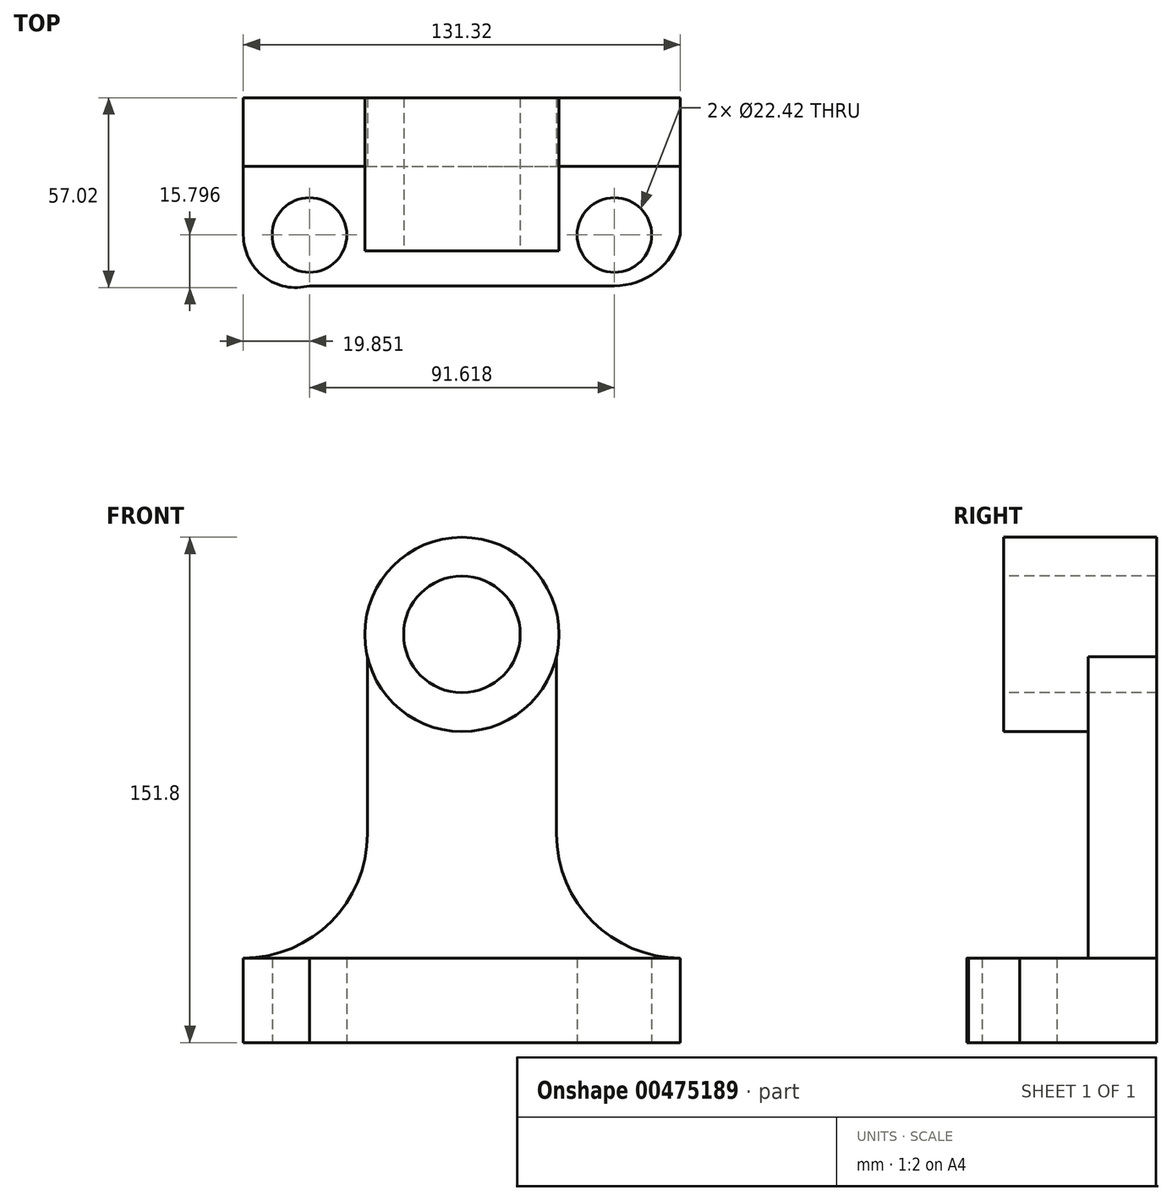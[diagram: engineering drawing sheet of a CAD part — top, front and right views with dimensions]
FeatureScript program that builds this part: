
annotation { "Feature Type Name" : "Feature", "Feature Type Description" : "" }
export const myFeature = defineFeature(function(context is Context, id is Id, definition is map)
    precondition{}
    {
        {
            var Q0;
            Q0=qCreatedBy(makeId("Top.planeOp"),FACE);
            var sketch = newSketch(context, id + "F0", { "sketchPlane" : qUnion([Q0])});
            skLineSegment(sketch, "E0.bottom", {"start": v(65.66, -20.61) * mm, "end": v(-65.66, -20.61) * mm});
            skLineSegment(sketch, "E0.top", {"start": v(65.66, 20.61) * mm, "end": v(-65.66, 20.61) * mm});
            skLineSegment(sketch, "E0.left", {"start": v(65.66, -20.61) * mm, "end": v(65.66, 20.61) * mm});
            skLineSegment(sketch, "E0.right", {"start": v(-65.66, -20.61) * mm, "end": v(-65.66, 20.61) * mm});
            skPoint(sketch, "E0.middle", {"position": v(0, 0) * mm});
            skLineSegment(sketch, "E1.bottom", {"start": v(45.8, -35.88) * mm, "end": v(-45.8, -35.88) * mm});
            skLineSegment(sketch, "E1.left", {"start": v(45.8, -35.88) * mm, "end": v(45.8, -20.61) * mm});
            skLineSegment(sketch, "E1.right", {"start": v(-45.8, -35.88) * mm, "end": v(-45.8, -20.61) * mm});
            skPoint(sketch, "E1.middle", {"position": v(0, -20.61) * mm});
            skPoint(sketch, "E1.top.end.orphan", {"position": v(-45.8, -5.34) * mm});
            skPoint(sketch, "E2.orphan", {"position": v(45.8, -5.34) * mm});
            skArc(sketch, "E3", {"start": v(45.8, -35.88) * mm, "mid": v(58.33, -31.62) * mm, "end": v(65.66, -20.61) * mm});
            skArc(sketch, "E4", {"start": v(-65.66, -20.61) * mm, "mid": v(-59.5, -33.14) * mm, "end": v(-45.8, -35.88) * mm});
            skCircle(sketch, "E5", {"center": v(45.8, -20.61) * mm, "radius": 11.2 * mm});
            skCircle(sketch, "E6", {"center": v(-45.8, -20.61) * mm, "radius": 11.2 * mm});
            skSolve(sketch);
        }
        {
            var Q0;
            {var subQ1=sQuery(id+"F0.wireOp",EDGE,"E1.bottom");Q0=makeQuery(id+"F0.imprint","IMPRINT",FACE,{"disambiguationData":[TD([[makeQuery(id+"F0.imprint","IMPRINT",EDGE,{"derivedFrom":subQ1}),-1.0]])]});}
            var Q1;
            {var subQ0=sQuery(id+"F0.wireOp",EDGE,"E4");Q1=makeQuery(id+"F0.imprint","IMPRINT",FACE,{"disambiguationData":[TD([[makeQuery(id+"F0.imprint","IMPRINT",EDGE,{"derivedFrom":subQ0}),1.0]])]});}
            var Q2;
            {var subQ0=sQuery(id+"F0.wireOp",EDGE,"E3");Q2=makeQuery(id+"F0.imprint","IMPRINT",FACE,{"disambiguationData":[TD([[makeQuery(id+"F0.imprint","IMPRINT",EDGE,{"derivedFrom":subQ0}),1.0]])]});}
            var Q3;
            Q3=makeQuery(id+"F0.imprint","IMPRINT",FACE,{"disambiguationData":[TD([[makeQuery(id+"F0.imprint","IMPRINT",EDGE,{"derivedFrom":sQuery(id+"F0.wireOp",EDGE,"E0.top")}),1.0]])]});
            extrude(context, id + "F1", {"entities" : qUnion([Q0, Q1, Q2, Q3]), "depth" : 25.4 * mm});
        }
        {
            var Q0;
            Q0=qCreatedBy(makeId("Front.planeOp"),FACE);
            var sketch = newSketch(context, id + "F2", { "sketchPlane" : qUnion([Q0])});
            skCircle(sketch, "E7", {"center": v(0, 122.62) * mm, "radius": 17.5 * mm});
            skCircle(sketch, "E8", {"center": v(0, 122.62) * mm, "radius": 29.18 * mm});
            skLineSegment(sketch, "E9.top", {"start": v(-28.4, 25.4) * mm, "end": v(28.4, 25.4) * mm});
            skLineSegment(sketch, "E9.left", {"start": v(-28.4, 115.9) * mm, "end": v(-28.4, 25.4) * mm});
            skLineSegment(sketch, "E9.right", {"start": v(28.4, 115.9) * mm, "end": v(28.4, 25.4) * mm});
            skArc(sketch, "E10", {"start": v(28.4, 62.67) * mm, "mid": v(39.3, 36.31) * mm, "end": v(65.66, 25.4) * mm});
            skLineSegment(sketch, "E11.0", {"start": v(45.8, 25.4) * mm, "end": v(-45.8, 25.4) * mm});
            skLineSegment(sketch, "E12.0", {"start": v(45.8, 25.4) * mm, "end": v(65.66, 25.4) * mm});
            skLineSegment(sketch, "E13.0", {"start": v(-65.66, 25.4) * mm, "end": v(-45.8, 25.4) * mm});
            skLineSegment(sketch, "E14.0.2", {"start": v(65.66, 25.4) * mm, "end": v(-65.66, 25.4) * mm});
            skLineSegment(sketch, "E14.0.5", {"start": v(-45.8, 25.4) * mm, "end": v(45.8, 25.4) * mm});
            skArc(sketch, "E15", {"start": v(-65.66, 25.4) * mm, "mid": v(-39.3, 36.31) * mm, "end": v(-28.4, 62.67) * mm});
            skSolve(sketch);
        }
        {
            var Q0;
            {var subQ0=sQuery(id+"F2.wireOp",EDGE,"E9.top");Q0=makeQuery(id+"F2.imprint","IMPRINT",FACE,{"disambiguationData":[TD([[makeQuery(id+"F2.imprint","IMPRINT",EDGE,{"derivedFrom":subQ0}),1.0]])]});}
            var Q1;
            {var subQ0=sQuery(id+"F2.wireOp",EDGE,"E10");Q1=makeQuery(id+"F2.imprint","IMPRINT",FACE,{"disambiguationData":[TD([[makeQuery(id+"F2.imprint","IMPRINT",EDGE,{"derivedFrom":subQ0}),-1.0]])]});}
            var Q2;
            {var subQ1=sQuery(id+"F2.wireOp",EDGE,"E8");var subQ4=sQuery(id+"F2.wireOp",EDGE,"E9.left");var subQ8=makeQuery(id+"F2.imprint","INTERSECT",VERTEX,{"derivedFrom":[subQ1,subQ4]});Q2=makeQuery(id+"F2.imprint","IMPRINT",FACE,{"disambiguationData":[TD([[makeQuery(id+"F2.imprint","IMPRINT",EDGE,{"disambiguationData":[TD([[subQ8,-1.0]])],"derivedFrom":subQ1}),-1.0]])]});}
            var Q3;
            {var subQ4=sQuery(id+"F2.wireOp",EDGE,"E13.0");Q3=makeQuery(id+"F2.imprint","IMPRINT",FACE,{"disambiguationData":[TD([[makeQuery(id+"F2.imprint","IMPRINT",EDGE,{"derivedFrom":subQ4}),1.0]])]});}
            var Q4;
            Q4=makeQuery(id+"F2.imprint","IMPRINT",FACE,{"disambiguationData":[TD([[makeQuery(id+"F2.imprint","IMPRINT",EDGE,{"derivedFrom":sQuery(id+"F2.wireOp",EDGE,"E7")}),-1.0]])]});
            var Q5;
            Q5=makeQuery(id+"F1.opExtrude","SWEPT_FACE",FACE,{"disambiguationData":[OSD([sQuery(id+"F0.wireOp",EDGE,"E0.top")])]});
            extrude(context, id + "F3", {"entities" : qUnion([Q0, Q1, Q2, Q3, Q4]), "operationType" : NewBodyOperationType.ADD, "endBound" : BoundingType.UP_TO_SURFACE, "oppositeDirection" : true, "endBoundEntityFace" : qUnion([Q5]), "depth" : 25.4 * mm});
        }
        {
            var Q0;
            Q0=makeQuery(id+"F2.imprint","IMPRINT",FACE,{"disambiguationData":[TD([[makeQuery(id+"F2.imprint","IMPRINT",EDGE,{"derivedFrom":sQuery(id+"F2.wireOp",EDGE,"E7")}),-1.0]])]});
            extrude(context, id + "F4", {"entities" : qUnion([Q0]), "operationType" : NewBodyOperationType.ADD, "depth" : 25.4 * mm});
        }
    });
